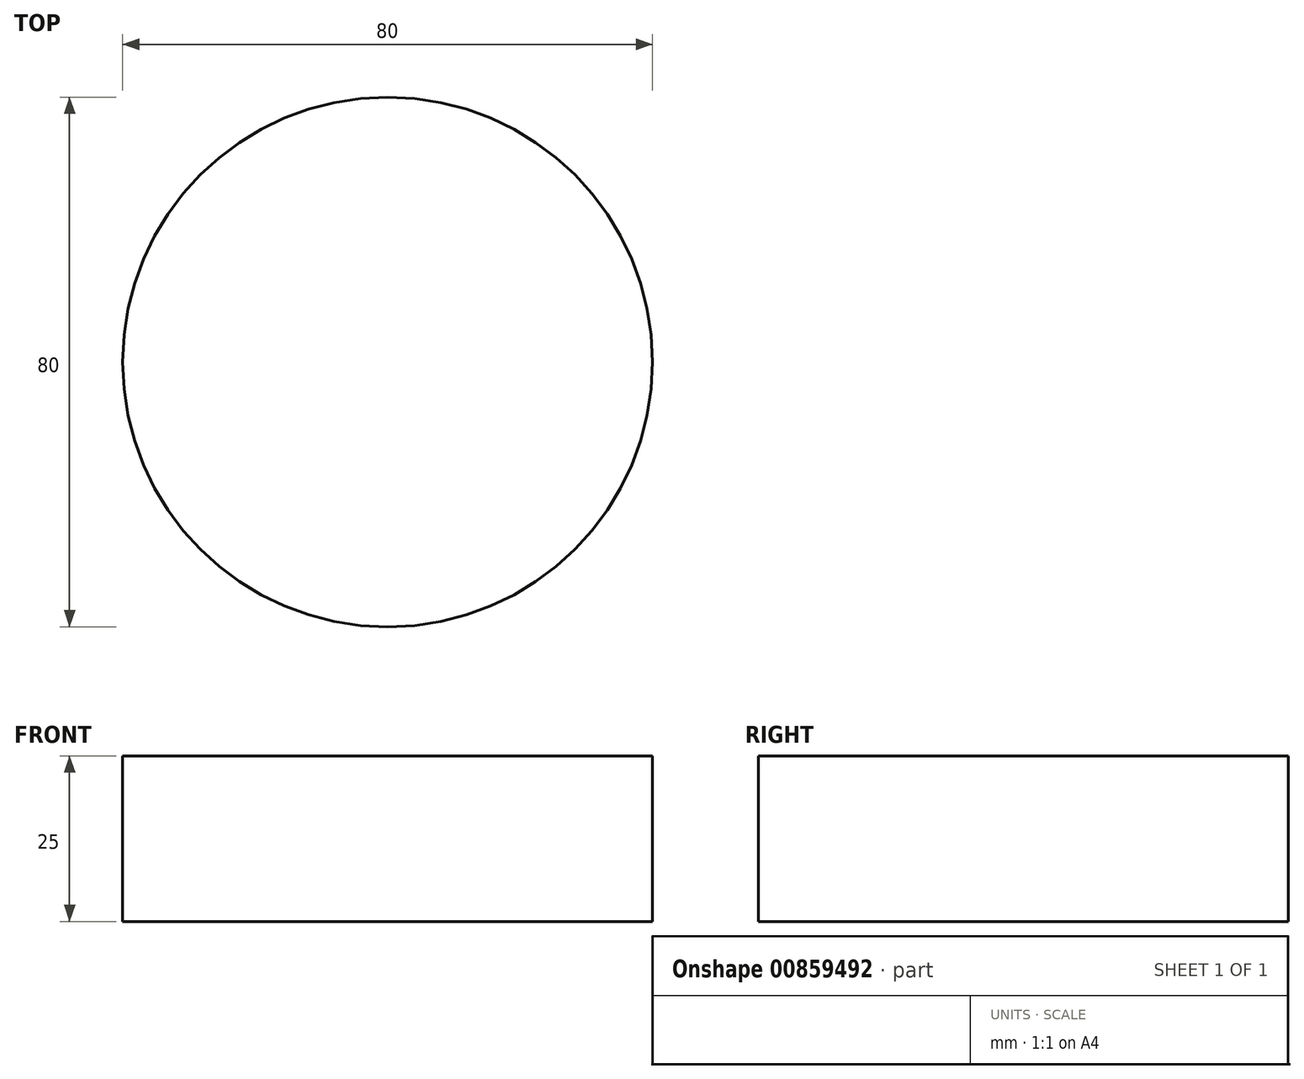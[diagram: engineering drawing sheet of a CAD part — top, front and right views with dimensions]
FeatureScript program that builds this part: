
annotation { "Feature Type Name" : "Feature", "Feature Type Description" : "" }
export const myFeature = defineFeature(function(context is Context, id is Id, definition is map)
    precondition{}
    {
        {
            var Q0;
            Q0=qCreatedBy(makeId("Top.planeOp"),FACE);
            var sketch = newSketch(context, id + "F0", { "sketchPlane" : qUnion([Q0])});
            skCircle(sketch, "E0", {"center": v(0, 0) * mm, "radius": 40 * mm});
            skSolve(sketch);
        }
        {
            var Q0;
            Q0=makeQuery(id+"F0.imprint","IMPRINT",FACE,{"disambiguationData":[TD([[makeQuery(id+"F0.imprint","IMPRINT",EDGE,{"derivedFrom":sQuery(id+"F0.wireOp",EDGE,"E0")}),1.0]])]});
            extrude(context, id + "F1", {"entities" : qUnion([Q0]), "depth" : 25 * mm, "offsetDistance" : 25 * mm});
        }
    });
